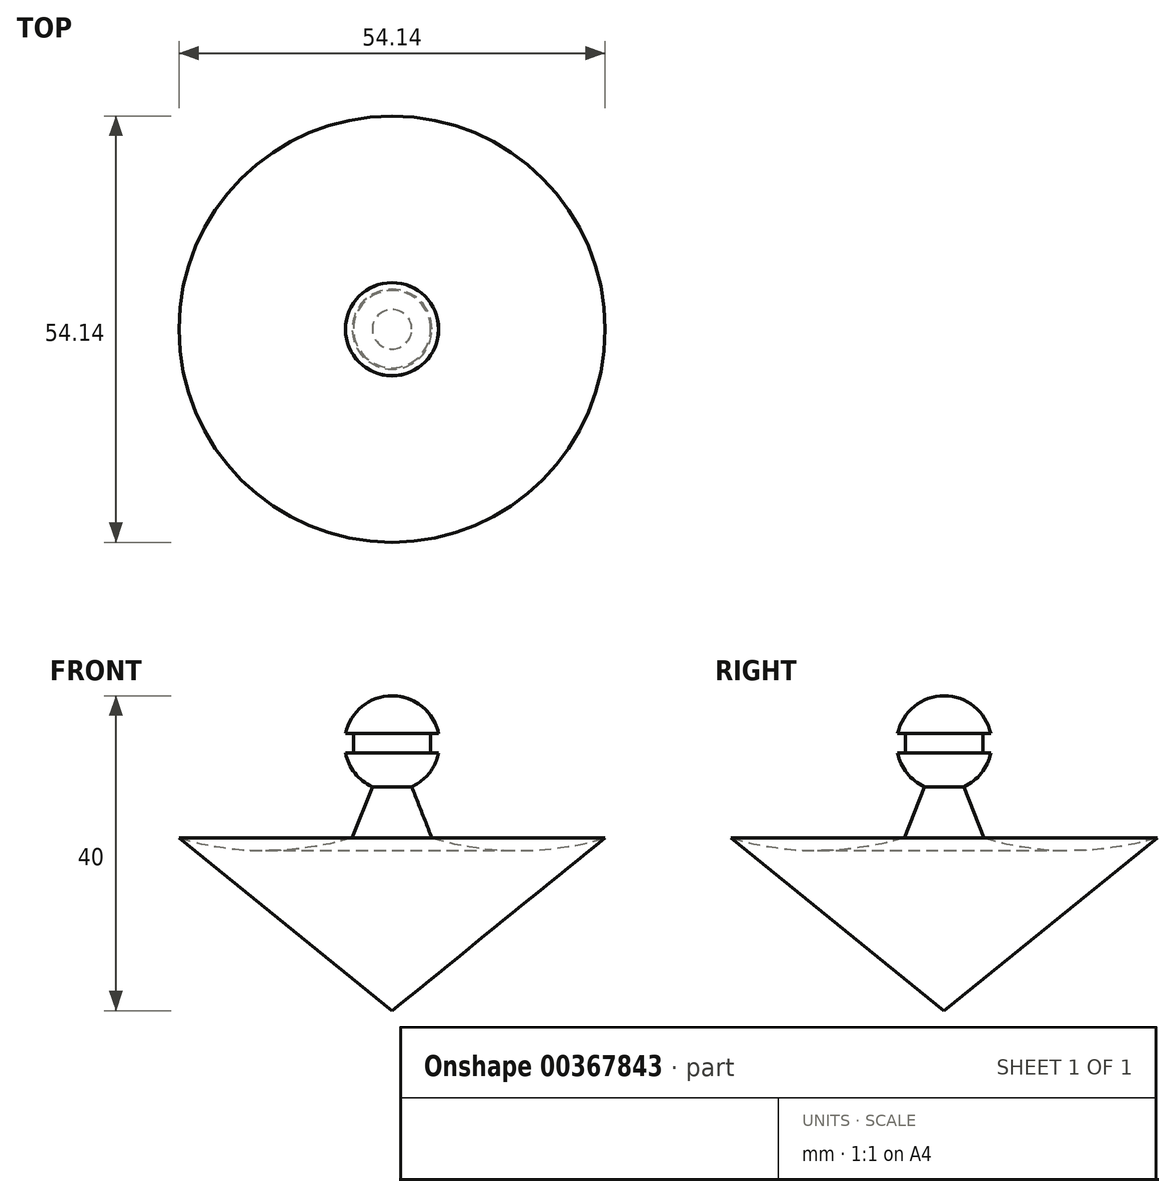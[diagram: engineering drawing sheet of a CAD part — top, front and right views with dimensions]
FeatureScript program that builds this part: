
annotation { "Feature Type Name" : "Feature", "Feature Type Description" : "" }
export const myFeature = defineFeature(function(context is Context, id is Id, definition is map)
    precondition{}
    {
        {
            var Q0;
            Q0=qCreatedBy(makeId("Front.planeOp"),FACE);
            var sketch = newSketch(context, id + "F0", { "sketchPlane" : qUnion([Q0])});
            skArc(sketch, "E0", {"start": v(-43.92, 22) * mm, "mid": v(-41.7, 23.73) * mm, "end": v(-40.5, 26.28) * mm});
            skLineSegment(sketch, "E1", {"start": v(-46.42, 33.55) * mm, "end": v(-46.42, -6.45) * mm});
            skLineSegment(sketch, "E2", {"start": v(-43.92, 22) * mm, "end": v(-41.35, 15.48) * mm});
            skLineSegment(sketch, "E3", {"start": v(-19.35, 15.48) * mm, "end": v(-46.42, -6.45) * mm});
            skArc(sketch, "E4", {"start": v(-41.35, 15.48) * mm, "mid": v(-30.35, 13.9) * mm, "end": v(-19.35, 15.48) * mm});
            skLineSegment(sketch, "E5.bottom", {"start": v(-40.51, 28.78) * mm, "end": v(-41.51, 28.78) * mm});
            skLineSegment(sketch, "E5.top", {"start": v(-40.51, 26.28) * mm, "end": v(-41.51, 26.28) * mm});
            skLineSegment(sketch, "E5.right", {"start": v(-41.51, 28.78) * mm, "end": v(-41.51, 26.28) * mm});
            skLineSegment(sketch, "E6", {"start": v(-40.51, 26.28) * mm, "end": v(-40.5, 26.28) * mm});
            skArc(sketch, "E7.trimOffspring", {"start": v(-40.51, 28.78) * mm, "mid": v(-42.63, 32.2) * mm, "end": v(-46.42, 33.55) * mm});
            skSolve(sketch);
        }
        {
            var Q0;
            Q0=makeQuery(id+"F0.imprint","IMPRINT",FACE,{"disambiguationData":[TD([[makeQuery(id+"F0.imprint","IMPRINT",EDGE,{"derivedFrom":sQuery(id+"F0.wireOp",EDGE,"E0")}),1.0]])]});
            var Q1;
            Q1=sQuery(id+"F0.wireOp",EDGE,"E1");
            revolve(context, id + "F1", {"entities" : qUnion([Q0]), "axis" : qUnion([Q1]), "revolveType" : RevolveType.FULL});
        }
    });
